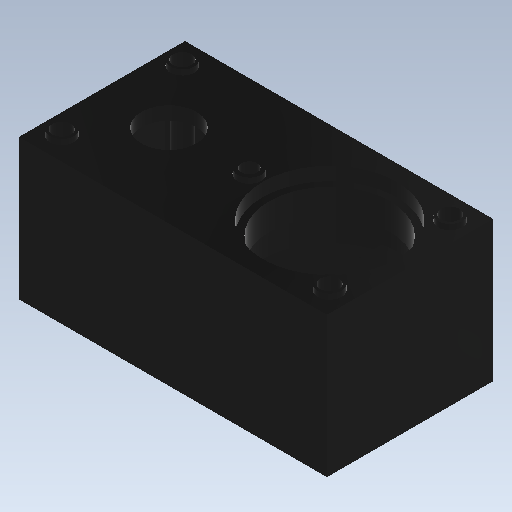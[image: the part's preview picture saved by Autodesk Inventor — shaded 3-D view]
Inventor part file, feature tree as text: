
AUTODESK INVENTOR PART (.ipt)
format: ipt  version: 2020 (Build 240168000, 168)  size: 253,440 bytes
history: native  units: mm
features: sketch x14, extrude x11, hole x3, projected_geometry x3, other x1, chamfer x1
ambient origin geometry x8: Origin, YZ Plane, XZ Plane, XY Plane, X Axis, Y Axis, Z Axis, Center Point
bodies: Body1 (feature_tree)
feature tree (33):
  other  "Твердое тело1"
  extrude  "Выдавливание1"  Depth=12.4mm
  extrude  "Выдавливание2"  Depth=23.0mm
  chamfer  "Фаска1"  Distance=10.5mm
  extrude  "Выдавливание3"  Depth=9.5mm TaperAngle=0.0deg
  extrude  "Выдавливание4"  Depth=1.5mm TaperAngle=45.0deg
  hole  "Отверстие1"  [1 undecoded]
  extrude  "Выдавливание5"  Depth=8.0mm
  extrude  "Выдавливание6"  Depth=1.0mm
  extrude  "Выдавливание7"  Depth=1.0mm
  extrude  "Выдавливание8"  Depth=4.0mm TaperAngle=0.0deg
  extrude  "Выдавливание9"  Depth=1.0mm TaperAngle=0.0deg
  extrude  "Выдавливание10"  Depth=10.0mm
  hole  "Отверстие2"  [1 undecoded]
  hole  "Отверстие3"  [1 undecoded]
  extrude  "Выдавливание11"  Depth=9.0mm
  sketch  "Эскиз1"
  sketch  "Эскиз2"
  projected_geometry  "Спроецированная петля1"
  sketch  "Эскиз3"
  sketch  "Эскиз4"
  sketch  "Эскиз5"
  sketch  "Эскиз6"
  sketch  "Эскиз7"
  projected_geometry  "Спроецированная петля2"
  sketch  "Эскиз8"
  projected_geometry  "Спроецированная петля3"
  sketch  "Эскиз9"
  sketch  "Эскиз10"
  sketch  "Эскиз11"
  sketch  "Эскиз12"
  sketch  "Эскиз13"
  sketch  "Эскиз14"
note: 3 required parameter values undecoded (feature->parameter linkage not recoverable at this tier; creation-order binding heuristic only, values carry confidence <= 0.55)
